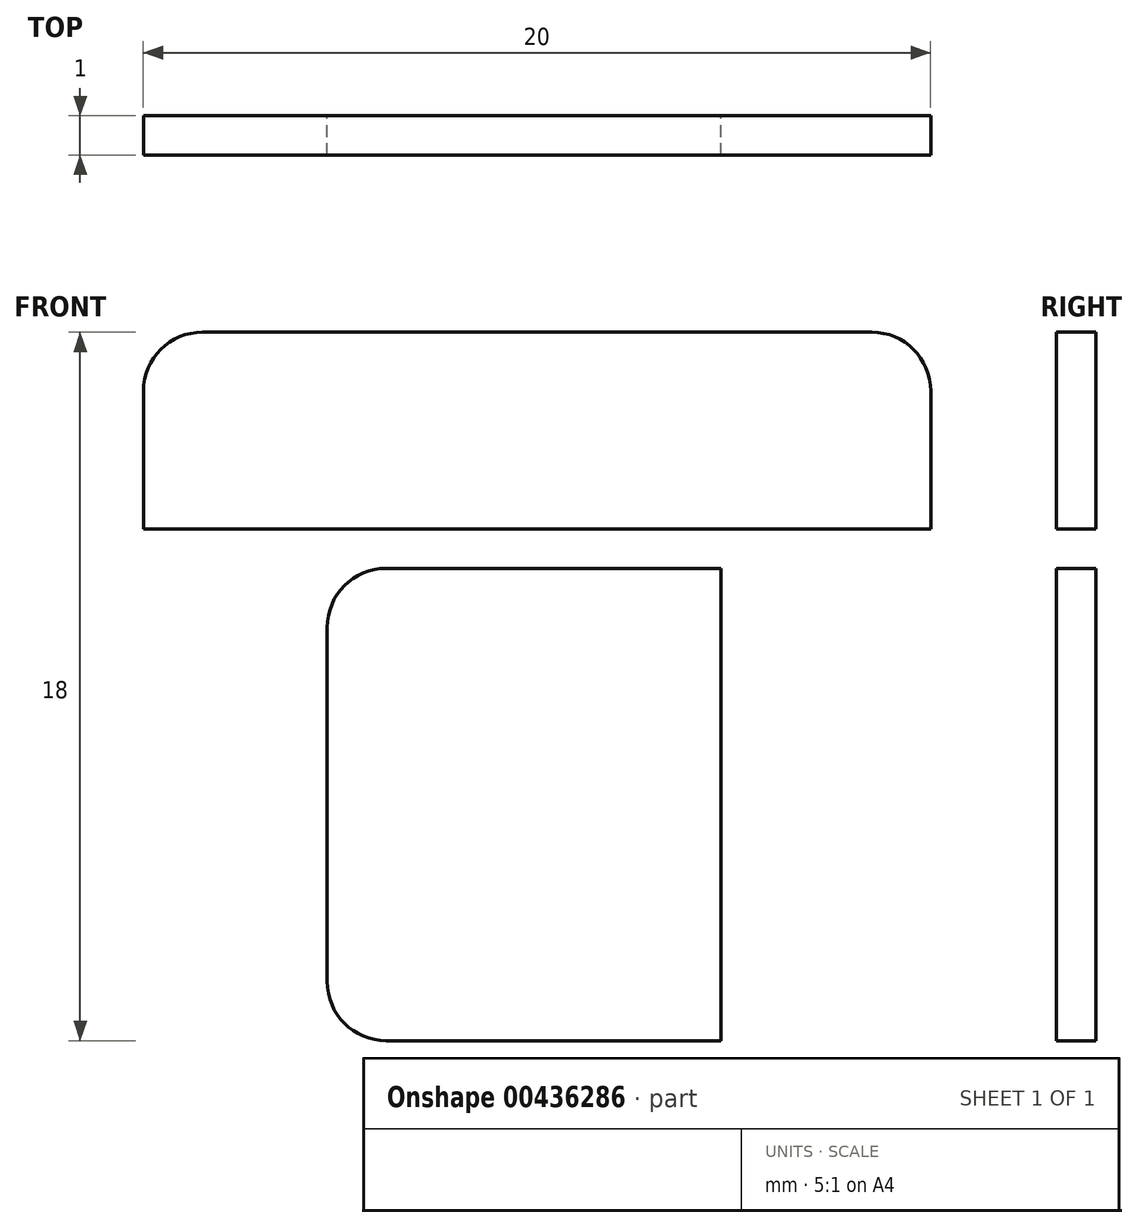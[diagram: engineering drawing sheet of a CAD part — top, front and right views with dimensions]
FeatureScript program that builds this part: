
annotation { "Feature Type Name" : "Feature", "Feature Type Description" : "" }
export const myFeature = defineFeature(function(context is Context, id is Id, definition is map)
    precondition{}
    {
        {
            var Q0;
            Q0=qCreatedBy(makeId("Front.planeOp"),FACE);
            var sketch = newSketch(context, id + "F0", { "sketchPlane" : qUnion([Q0])});
            skLineSegment(sketch, "E0.bottom", {"start": v(7.83, -19.56) * mm, "end": v(24.83, -19.56) * mm});
            skLineSegment(sketch, "E0.top", {"start": v(6.33, -24.56) * mm, "end": v(26.33, -24.56) * mm});
            skLineSegment(sketch, "E0.left", {"start": v(6.33, -21.06) * mm, "end": v(6.33, -24.56) * mm});
            skLineSegment(sketch, "E0.right", {"start": v(26.33, -21.06) * mm, "end": v(26.33, -24.56) * mm});
            skLineSegment(sketch, "E1.bottom", {"start": v(12.5, -25.56) * mm, "end": v(21, -25.56) * mm});
            skLineSegment(sketch, "E1.top", {"start": v(12.5, -37.56) * mm, "end": v(21, -37.56) * mm});
            skLineSegment(sketch, "E1.left", {"start": v(11, -27.06) * mm, "end": v(11, -36.06) * mm});
            skLineSegment(sketch, "E1.right", {"start": v(21, -25.56) * mm, "end": v(21, -37.56) * mm});
            skPoint(sketch, "E2.visualSharp", {"position": v(6.33, -19.56) * mm});
            skArc(sketch, "E2.filletArc", {"start": v(7.83, -19.56) * mm, "mid": v(6.77, -20) * mm, "end": v(6.33, -21.06) * mm});
            skPoint(sketch, "E3.visualSharp", {"position": v(26.33, -19.56) * mm});
            skArc(sketch, "E3.filletArc", {"start": v(26.33, -21.06) * mm, "mid": v(25.9, -20) * mm, "end": v(24.83, -19.56) * mm});
            skPoint(sketch, "E4.visualSharp", {"position": v(11, -25.56) * mm});
            skArc(sketch, "E4.filletArc", {"start": v(12.5, -25.56) * mm, "mid": v(11.44, -26) * mm, "end": v(11, -27.06) * mm});
            skPoint(sketch, "E5.visualSharp", {"position": v(11, -37.56) * mm});
            skArc(sketch, "E5.filletArc", {"start": v(11, -36.06) * mm, "mid": v(11.44, -37.12) * mm, "end": v(12.5, -37.56) * mm});
            skSolve(sketch);
        }
        {
            var Q0;
            Q0=makeQuery(id+"F0.imprint","IMPRINT",FACE,{"disambiguationData":[TD([[makeQuery(id+"F0.imprint","IMPRINT",EDGE,{"derivedFrom":sQuery(id+"F0.wireOp",EDGE,"E0.bottom")}),-1.0]])]});
            var Q1;
            Q1=makeQuery(id+"F0.imprint","IMPRINT",FACE,{"disambiguationData":[TD([[makeQuery(id+"F0.imprint","IMPRINT",EDGE,{"derivedFrom":sQuery(id+"F0.wireOp",EDGE,"E1.bottom")}),-1.0]])]});
            extrude(context, id + "F1", {"entities" : qUnion([Q0, Q1]), "depth" : 1 * mm});
        }
    });
